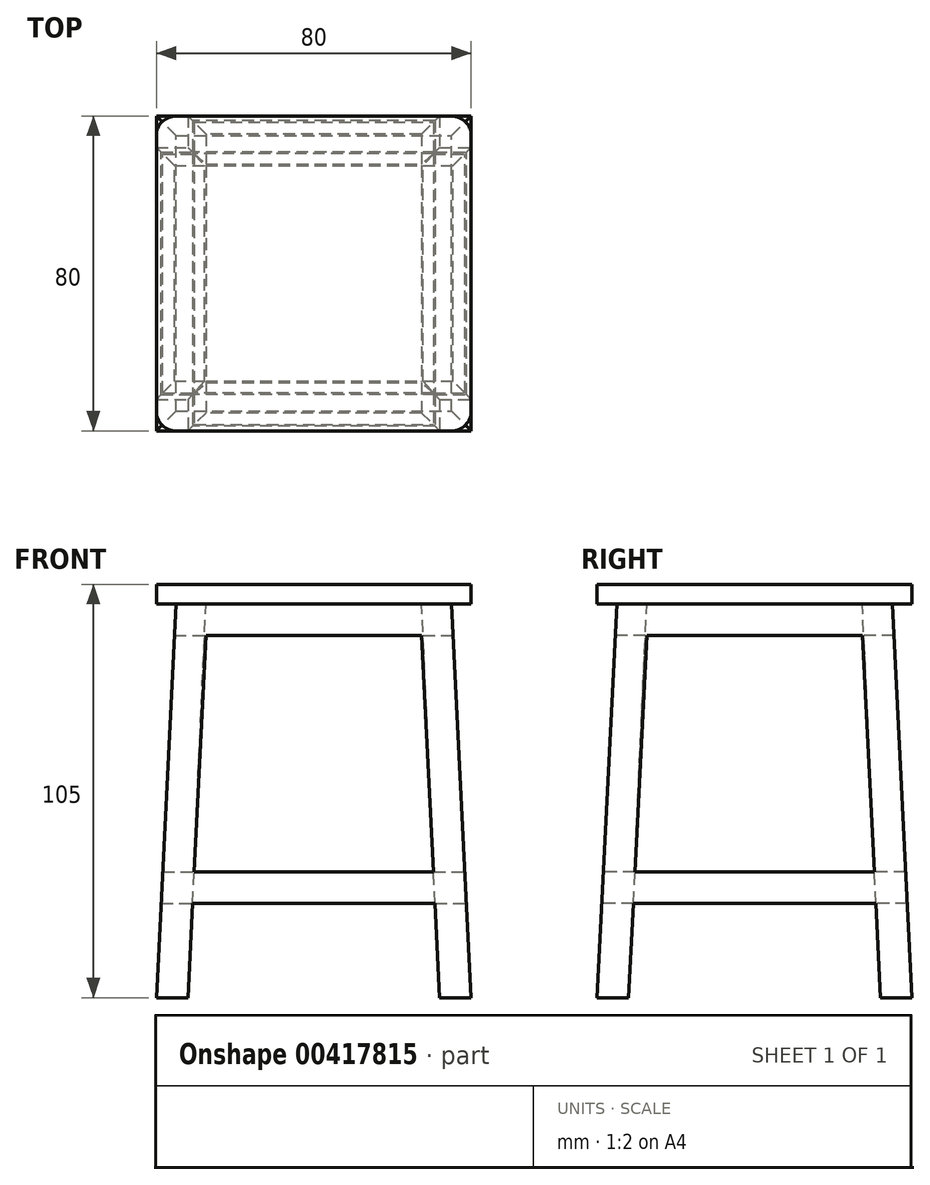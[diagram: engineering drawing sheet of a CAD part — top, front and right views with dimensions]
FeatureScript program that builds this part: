
annotation { "Feature Type Name" : "Feature", "Feature Type Description" : "" }
export const myFeature = defineFeature(function(context is Context, id is Id, definition is map)
    precondition{}
    {
        {
            var Q0;
            Q0=qCreatedBy(makeId("Top.planeOp"),FACE);
            var sketch = newSketch(context, id + "F0", { "sketchPlane" : qUnion([Q0])});
            skLineSegment(sketch, "E0.bottom", {"start": v(-35, -35) * mm, "end": v(35, -35) * mm});
            skLineSegment(sketch, "E0.top", {"start": v(-35, 35) * mm, "end": v(35, 35) * mm});
            skLineSegment(sketch, "E0.left", {"start": v(-35, -35) * mm, "end": v(-35, 35) * mm});
            skLineSegment(sketch, "E0.right", {"start": v(35, -35) * mm, "end": v(35, 35) * mm});
            skPoint(sketch, "E0.middle", {"position": v(0, 0) * mm});
            skSolve(sketch);
        }
        {
            var Q0;
            Q0=qCreatedBy(makeId("Top.planeOp"),FACE);
            cPlane(context, id + "F1", {"entities" : qUnion([Q0]), "cplaneType" : CPlaneType.OFFSET, "offset" : 100 * mm, "oppositeDirection" : true, "width" : 150 * mm, "height" : 150 * mm});
        }
        {
            var Q0;
            Q0=qCreatedBy(id+"F1.planeOp",FACE);
            var sketch = newSketch(context, id + "F2", { "sketchPlane" : qUnion([Q0])});
            skLineSegment(sketch, "E1.bottom", {"start": v(-40, -40) * mm, "end": v(40, -40) * mm});
            skLineSegment(sketch, "E1.top", {"start": v(-40, 40) * mm, "end": v(40, 40) * mm});
            skLineSegment(sketch, "E1.left", {"start": v(-40, -40) * mm, "end": v(-40, 40) * mm});
            skLineSegment(sketch, "E1.right", {"start": v(40, -40) * mm, "end": v(40, 40) * mm});
            skPoint(sketch, "E1.middle", {"position": v(0, 0) * mm});
            skSolve(sketch);
        }
        {
            var Q0;
            Q0=makeQuery(id+"F0.imprint","IMPRINT",FACE,{"disambiguationData":[TD([[makeQuery(id+"F0.imprint","IMPRINT",EDGE,{"derivedFrom":sQuery(id+"F0.wireOp",EDGE,"E0.bottom")}),1.0]])]});
            var Q1;
            Q1=makeQuery(id+"F2.imprint","IMPRINT",FACE,{"disambiguationData":[TD([[makeQuery(id+"F2.imprint","IMPRINT",EDGE,{"derivedFrom":sQuery(id+"F2.wireOp",EDGE,"E1.bottom")}),1.0]])]});
            loft(context, id + "F3", {"sheetProfilesArray" : [{ "sheetProfileEntities" : qUnion([Q0]) }, { "sheetProfileEntities" : qUnion([Q1]) }]});
        }
        {
            var Q0;
            Q0=qCreatedBy(makeId("Front.planeOp"),FACE);
            var sketch = newSketch(context, id + "F4", { "sketchPlane" : qUnion([Q0])});
            skLineSegment(sketch, "E2", {"start": v(32, -100) * mm, "end": v(30.8, -76) * mm});
            skLineSegment(sketch, "E3", {"start": v(-32, -100) * mm, "end": v(-30.8, -76) * mm});
            skLineSegment(sketch, "E4", {"start": v(-27.4, -8) * mm, "end": v(27.4, -8) * mm});
            skLineSegment(sketch, "E5", {"start": v(30.4, -68) * mm, "end": v(-30.4, -68) * mm});
            skLineSegment(sketch, "E6", {"start": v(-30.8, -76) * mm, "end": v(30.8, -76) * mm});
            skLineSegment(sketch, "E7", {"start": v(30.8, -76) * mm, "end": v(32, -100) * mm});
            skLineSegment(sketch, "E8", {"start": v(32, -100) * mm, "end": v(-32, -100) * mm});
            skPoint(sketch, "E9.0.start.orphan", {"position": v(35, 0) * mm});
            skPoint(sketch, "E10.0.start.orphan", {"position": v(-35, 0) * mm});
            skPoint(sketch, "E11.0.start.orphan", {"position": v(-40, -100) * mm});
            skLineSegment(sketch, "E12.trimOffspring", {"start": v(30.4, -68) * mm, "end": v(27.4, -8) * mm});
            skLineSegment(sketch, "E13.trimOffspring", {"start": v(-30.4, -68) * mm, "end": v(-27.4, -8) * mm});
            skPoint(sketch, "E14.trimOffspring.end.orphan", {"position": v(40, -100) * mm});
            skSolve(sketch);
        }
        {
            var Q0;
            Q0 = qSketchRegion(id + "F4", true);
            extrude(context, id + "F5", {"entities" : qUnion([Q0]), "operationType" : NewBodyOperationType.REMOVE, "endBound" : BoundingType.SYMMETRIC, "oppositeDirection" : true, "depth" : 125.6 * mm});
        }
        {
            var Q0;
            Q0=qCreatedBy(makeId("Right.planeOp"),FACE);
            var sketch = newSketch(context, id + "F6", { "sketchPlane" : qUnion([Q0])});
            skLineSegment(sketch, "E15.0.1", {"start": v(32, -100) * mm, "end": v(-32, -100) * mm});
            skLineSegment(sketch, "E16", {"start": v(32, -100) * mm, "end": v(30.8, -76) * mm});
            skLineSegment(sketch, "E17", {"start": v(27.4, -8) * mm, "end": v(-27.4, -8) * mm});
            skLineSegment(sketch, "E18", {"start": v(-27.4, -8) * mm, "end": v(-30.4, -68) * mm});
            skLineSegment(sketch, "E19", {"start": v(30.4, -68) * mm, "end": v(-30.4, -68) * mm});
            skLineSegment(sketch, "E20", {"start": v(30.8, -76) * mm, "end": v(-30.8, -76) * mm});
            skLineSegment(sketch, "E21.trimOffspring", {"start": v(-30.8, -76) * mm, "end": v(-32, -100) * mm});
            skLineSegment(sketch, "E22.trimOffspring", {"start": v(30.4, -68) * mm, "end": v(27.4, -8) * mm});
            skPoint(sketch, "E15.0.0.end.orphan", {"position": v(40, -100) * mm});
            skPoint(sketch, "E15.0.2.start.orphan", {"position": v(-40, -100) * mm});
            skPoint(sketch, "E15.0.3.end.orphan", {"position": v(35, 0) * mm});
            skPoint(sketch, "E15.0.3.start.orphan", {"position": v(-35, 0) * mm});
            skSolve(sketch);
        }
        {
            var Q0;
            Q0 = qSketchRegion(id + "F6", true);
            extrude(context, id + "F7", {"entities" : qUnion([Q0]), "operationType" : NewBodyOperationType.REMOVE, "endBound" : BoundingType.SYMMETRIC, "oppositeDirection" : true, "depth" : 192 * mm});
        }
        {
            var Q0;
            Q0=makeQuery(id+"F7.boolean.opBoolean","MERGE",FACE,{"derivedFrom":[makeQuery(id+"F5.boolean.opBoolean","COPY",FACE,{"derivedFrom":makeQuery(id+"F5.opExtrude","SWEPT_FACE",FACE,{"disambiguationData":[OSD([sQuery(id+"F4.wireOp",EDGE,"E6")])]})}),makeQuery(id+"F7.opExtrude","SWEPT_FACE",FACE,{"disambiguationData":[OSD([sQuery(id+"F6.wireOp",EDGE,"E20")])]})]});
            var sketch = newSketch(context, id + "F8", { "sketchPlane" : qUnion([Q0])});
            skLineSegment(sketch, "E23.bottom", {"start": v(30.8, -30.8) * mm, "end": v(-30.8, -30.8) * mm});
            skLineSegment(sketch, "E23.top", {"start": v(30.8, 30.8) * mm, "end": v(-30.8, 30.8) * mm});
            skLineSegment(sketch, "E23.left", {"start": v(30.8, -30.8) * mm, "end": v(30.8, 30.8) * mm});
            skLineSegment(sketch, "E23.right", {"start": v(-30.8, -30.8) * mm, "end": v(-30.8, 30.8) * mm});
            skPoint(sketch, "E23.middle", {"position": v(0, 0) * mm});
            skSolve(sketch);
        }
        {
            var Q0;
            Q0=makeQuery(id+"F3.opLoft","CAP_FACE",FACE,{"disambiguationData":[OSD([makeQuery(id+"F0.imprint","IMPRINT",FACE,{"disambiguationData":[TD([[makeQuery(id+"F0.imprint","IMPRINT",EDGE,{"derivedFrom":sQuery(id+"F0.wireOp",EDGE,"E0.bottom")}),1.0]])]})])],"isStart":true});
            var sketch = newSketch(context, id + "F9", { "sketchPlane" : qUnion([Q0])});
            skLineSegment(sketch, "E24.bottom", {"start": v(-27.4, 27.4) * mm, "end": v(27.4, 27.4) * mm});
            skLineSegment(sketch, "E24.top", {"start": v(-27.4, -27.4) * mm, "end": v(27.4, -27.4) * mm});
            skLineSegment(sketch, "E24.left", {"start": v(-27.4, 27.4) * mm, "end": v(-27.4, -27.4) * mm});
            skLineSegment(sketch, "E24.right", {"start": v(27.4, 27.4) * mm, "end": v(27.4, -27.4) * mm});
            skPoint(sketch, "E24.middle", {"position": v(0, 0) * mm});
            skPoint(sketch, "E25.0", {"position": v(-27.4, 27.4) * mm});
            skSolve(sketch);
        }
        {
            var Q1;
            Q1=makeQuery(id+"F8.imprint","IMPRINT",FACE,{"disambiguationData":[TD([[makeQuery(id+"F8.imprint","IMPRINT",EDGE,{"derivedFrom":sQuery(id+"F8.wireOp",EDGE,"E23.bottom")}),-1.0]])]});
            var Q2;
            Q2=makeQuery(id+"F9.imprint","IMPRINT",FACE,{"disambiguationData":[TD([[makeQuery(id+"F9.imprint","IMPRINT",EDGE,{"derivedFrom":sQuery(id+"F9.wireOp",EDGE,"E24.bottom")}),-1.0]])]});
            loft(context, id + "F10", {"operationType" : NewBodyOperationType.REMOVE, "sheetProfilesArray" : [{ "sheetProfileEntities" : qUnion([Q1]) }, { "sheetProfileEntities" : qUnion([Q2]) }]});
        }
        {
            var Q0;
            Q0=makeQuery(id+"F3.opLoft","CAP_FACE",FACE,{"disambiguationData":[OSD([makeQuery(id+"F0.imprint","IMPRINT",FACE,{"disambiguationData":[TD([[makeQuery(id+"F0.imprint","IMPRINT",EDGE,{"derivedFrom":sQuery(id+"F0.wireOp",EDGE,"E0.bottom")}),1.0]])]})])],"isStart":true});
            var sketch = newSketch(context, id + "F11", { "sketchPlane" : qUnion([Q0])});
            skLineSegment(sketch, "E26.bottom", {"start": v(-40, -40) * mm, "end": v(40, -40) * mm});
            skLineSegment(sketch, "E26.top", {"start": v(-40, 40) * mm, "end": v(40, 40) * mm});
            skLineSegment(sketch, "E26.left", {"start": v(-40, -40) * mm, "end": v(-40, 40) * mm});
            skLineSegment(sketch, "E26.right", {"start": v(40, -40) * mm, "end": v(40, 40) * mm});
            skPoint(sketch, "E26.middle", {"position": v(0, 0) * mm});
            skSolve(sketch);
        }
        {
            var Q0;
            Q0 = qSketchRegion(id + "F11", true);
            extrude(context, id + "F12", {"entities" : qUnion([Q0]), "operationType" : NewBodyOperationType.ADD, "depth" : 5 * mm});
        }
        {
            var Q0;
            Q0=makeQuery(id+"F12.opExtrude","SWEPT_EDGE",EDGE,{"disambiguationData":[OSD([sQuery(id+"F11.wireOp",EDGE,"E26.top"),sQuery(id+"F11.wireOp",EDGE,"E26.left")])]});
            var Q1;
            Q1=makeQuery(id+"F12.opExtrude","SWEPT_EDGE",EDGE,{"disambiguationData":[OSD([sQuery(id+"F11.wireOp",EDGE,"E26.bottom"),sQuery(id+"F11.wireOp",EDGE,"E26.left")])]});
            var Q2;
            Q2=makeQuery(id+"F12.opExtrude","SWEPT_EDGE",EDGE,{"disambiguationData":[OSD([sQuery(id+"F11.wireOp",EDGE,"E26.bottom"),sQuery(id+"F11.wireOp",EDGE,"E26.right")])]});
            var Q3;
            Q3=makeQuery(id+"F12.opExtrude","SWEPT_EDGE",EDGE,{"disambiguationData":[OSD([sQuery(id+"F11.wireOp",EDGE,"E26.top"),sQuery(id+"F11.wireOp",EDGE,"E26.right")])]});
            fillet(context, id + "F13", {"entities" : qUnion([Q0, Q1, Q2, Q3]), "radius" : 5 * mm, "tangentPropagation" : true, "allowEdgeOverflow" : false});
        }
    });
